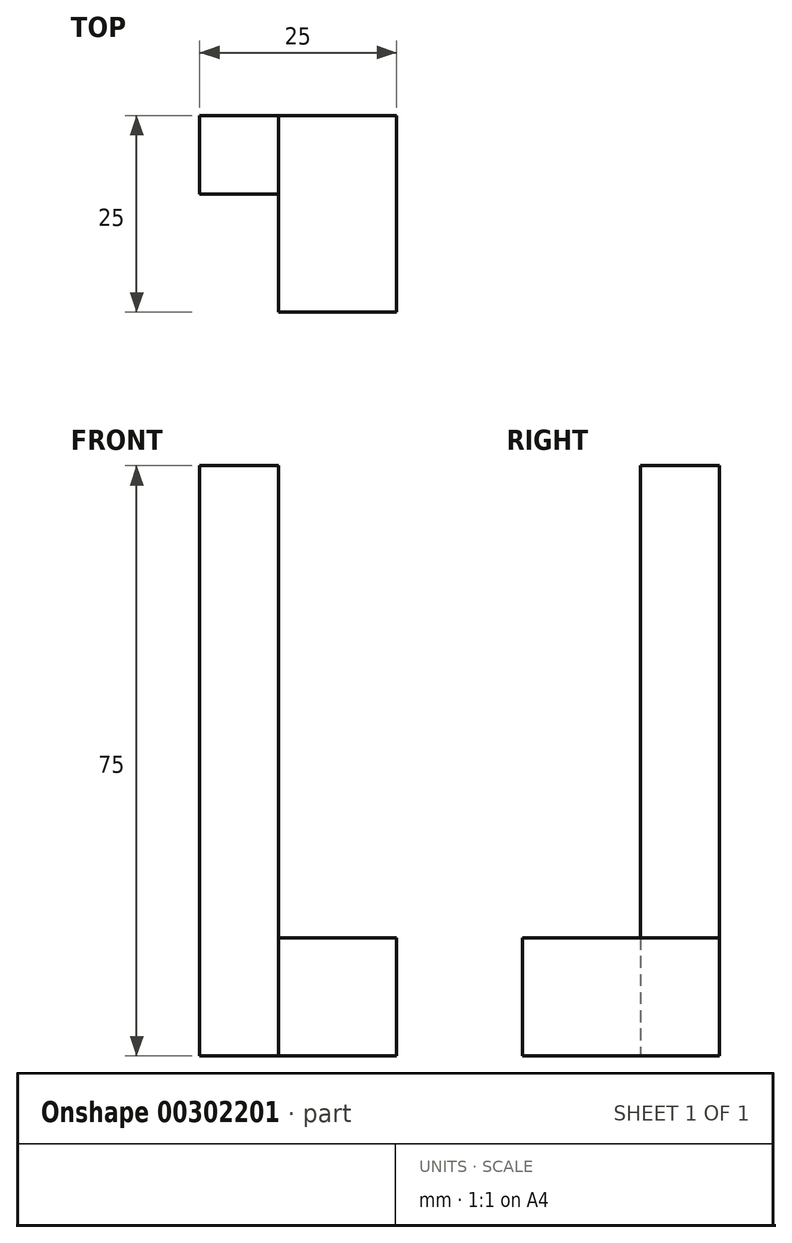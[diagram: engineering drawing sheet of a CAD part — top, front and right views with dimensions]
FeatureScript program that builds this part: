
annotation { "Feature Type Name" : "Feature", "Feature Type Description" : "" }
export const myFeature = defineFeature(function(context is Context, id is Id, definition is map)
    precondition{}
    {
        {
            var Q0;
            Q0=qCreatedBy(makeId("Front.planeOp"),FACE);
            var sketch = newSketch(context, id + "F0", { "sketchPlane" : qUnion([Q0])});
            skLineSegment(sketch, "E0.bottom", {"start": v(-58.8, 51.01) * mm, "end": v(-48.8, 51.01) * mm});
            skLineSegment(sketch, "E0.top", {"start": v(-58.8, -23.99) * mm, "end": v(-48.8, -23.99) * mm});
            skLineSegment(sketch, "E0.left", {"start": v(-58.8, 51.01) * mm, "end": v(-58.8, -23.99) * mm});
            skLineSegment(sketch, "E0.right", {"start": v(-48.8, 51.01) * mm, "end": v(-48.8, -23.99) * mm});
            skLineSegment(sketch, "E1.bottom", {"start": v(-48.8, -23.99) * mm, "end": v(-33.8, -23.99) * mm});
            skLineSegment(sketch, "E1.top", {"start": v(-48.8, -8.99) * mm, "end": v(-33.8, -8.99) * mm});
            skLineSegment(sketch, "E1.left", {"start": v(-48.8, -23.99) * mm, "end": v(-48.8, -8.99) * mm});
            skLineSegment(sketch, "E1.right", {"start": v(-33.8, -23.99) * mm, "end": v(-33.8, -8.99) * mm});
            skLineSegment(sketch, "E2.bottom", {"start": v(-33.8, -23.99) * mm, "end": v(22.52, -23.99) * mm});
            skLineSegment(sketch, "E2.top", {"start": v(-33.8, 24.78) * mm, "end": v(22.52, 24.78) * mm});
            skLineSegment(sketch, "E2.left", {"start": v(-33.8, -23.99) * mm, "end": v(-33.8, 24.78) * mm});
            skLineSegment(sketch, "E2.right", {"start": v(22.52, -23.99) * mm, "end": v(22.52, 24.78) * mm});
            skLineSegment(sketch, "E3.bottom", {"start": v(16.2, 25.42) * mm, "end": v(61.2, 25.42) * mm});
            skLineSegment(sketch, "E3.top", {"start": v(16.2, 10.42) * mm, "end": v(61.2, 10.42) * mm});
            skLineSegment(sketch, "E3.left", {"start": v(16.2, 25.42) * mm, "end": v(16.2, 10.42) * mm});
            skLineSegment(sketch, "E3.right", {"start": v(61.2, 25.42) * mm, "end": v(61.2, 10.42) * mm});
            skSolve(sketch);
        }
        {
            var Q0;
            Q0=makeQuery(id+"F0.imprint","IMPRINT",FACE,{"disambiguationData":[TD([[makeQuery(id+"F0.imprint","IMPRINT",EDGE,{"derivedFrom":sQuery(id+"F0.wireOp",EDGE,"E0.bottom")}),-1.0]])]});
            extrude(context, id + "F1", {"entities" : qUnion([Q0]), "depth" : 10 * mm});
        }
        {
            var Q0;
            {var subQ0=sQuery(id+"F0.wireOp",EDGE,"E1.bottom");Q0=makeQuery(id+"F0.imprint","IMPRINT",FACE,{"disambiguationData":[TD([[makeQuery(id+"F0.imprint","IMPRINT",EDGE,{"derivedFrom":subQ0}),1.0]])]});}
            extrude(context, id + "F2", {"entities" : qUnion([Q0]), "operationType" : NewBodyOperationType.ADD, "depth" : 25 * mm});
        }
    });
